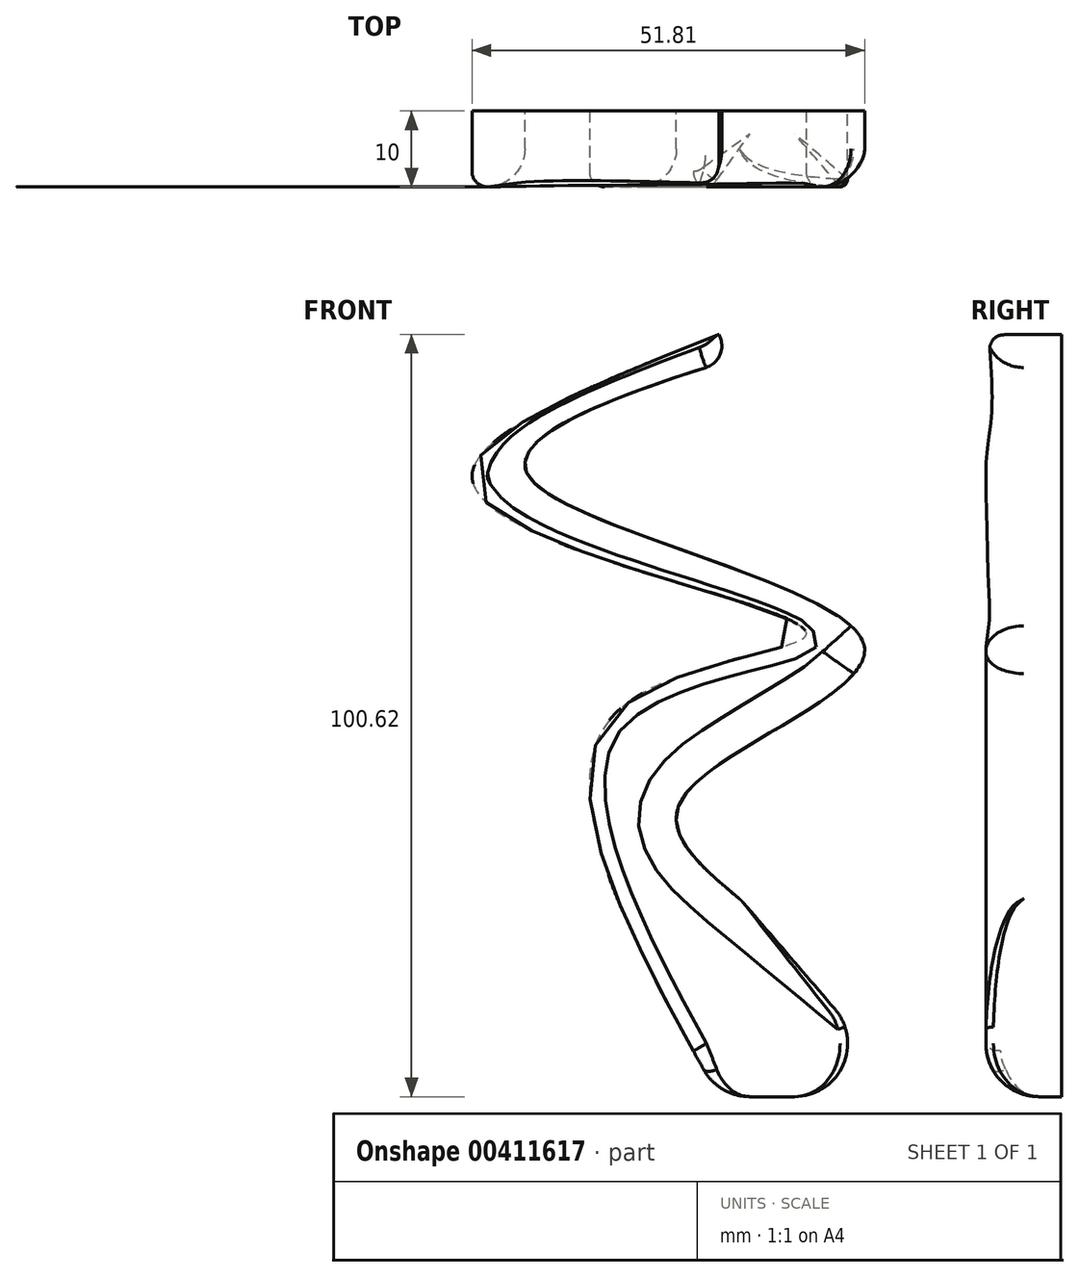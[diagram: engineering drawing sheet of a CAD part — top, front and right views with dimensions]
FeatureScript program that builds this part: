
annotation { "Feature Type Name" : "Feature", "Feature Type Description" : "" }
export const myFeature = defineFeature(function(context is Context, id is Id, definition is map)
    precondition{}
    {
        {
            var Q0;
            Q0=qCreatedBy(makeId("Front.planeOp"),FACE);
            var sketch = newSketch(context, id + "F0", { "sketchPlane" : qUnion([Q0])});
            skFitSpline(sketch, "E0", {"points": [v(0, 0) * mm, v(-32.55, -18.47) * mm, v(-11.86, -30.76) * mm, v(11.43, -39.81) * mm, v(-13.8, -50.16) * mm, v(0, -100.62) * mm], "startDerivative": vector(-224.38, -89.25) * mm, "endDerivative": vector(135.1, -241.68) * mm});
            skLineSegment(sketch, "E1", {"start": v(0, -100.62) * mm, "end": v(25.25, -100.62) * mm});
            skLineSegment(sketch, "E2", {"start": v(25.25, -100.62) * mm, "end": v(3.02, -74.74) * mm});
            skPoint(sketch, "E3.4.internal.snap0", {"position": v(12.63, -64.84) * mm});
            skFitSpline(sketch, "E3", {"points": [v(3.02, -74.74) * mm, v(-4.74, -61.16) * mm, v(19.2, -41.1) * mm, v(-24.8, -19.12) * mm, v(12.63, 0) * mm], "startDerivative": vector(-94.06, 77.83) * mm, "endDerivative": vector(227.32, 67.7) * mm});
            skLineSegment(sketch, "E4", {"start": v(0, 0) * mm, "end": v(12.63, 0) * mm});
            skSolve(sketch);
        }
        {
            var Q0;
            Q0=makeQuery(id+"F0.imprint","IMPRINT",FACE,{"disambiguationData":[TD([[makeQuery(id+"F0.imprint","IMPRINT",EDGE,{"derivedFrom":sQuery(id+"F0.wireOp",EDGE,"E0")}),1.0]])]});
            extrude(context, id + "F1", {"entities" : qUnion([Q0]), "depth" : 10 * mm});
        }
        {
            var Q0;
            Q0=makeQuery(id+"F1.opExtrude","CAP_EDGE",EDGE,{"disambiguationData":[OSD([sQuery(id+"F0.wireOp",EDGE,"E2")])],"isStart":false});
            fillet(context, id + "F2", {"entities" : qUnion([Q0]), "radius" : 1 * mm, "tangentPropagation" : true, "allowEdgeOverflow" : false});
        }
        {
            var Q0;
            Q0=makeQuery(id+"F1.opExtrude","CAP_EDGE",EDGE,{"disambiguationData":[OSD([sQuery(id+"F0.wireOp",EDGE,"E0")])],"isStart":false});
            fillet(context, id + "F3", {"entities" : qUnion([Q0]), "radius" : 2 * mm, "tangentPropagation" : true, "allowEdgeOverflow" : false});
        }
        {
            var Q0;
            Q0=makeQuery(id+"F1.opExtrude","CAP_EDGE",EDGE,{"disambiguationData":[OSD([sQuery(id+"F0.wireOp",EDGE,"E3")])],"isStart":false});
            fillet(context, id + "F4", {"entities" : qUnion([Q0]), "radius" : 5 * mm, "tangentPropagation" : true, "allowEdgeOverflow" : false});
        }
        {
            var Q0;
            Q0=makeQuery(id+"F1.opExtrude","CAP_EDGE",EDGE,{"disambiguationData":[OSD([sQuery(id+"F0.wireOp",EDGE,"E1")])],"isStart":false});
            fillet(context, id + "F5", {"entities" : qUnion([Q0]), "radius" : 7 * mm, "tangentPropagation" : true, "allowEdgeOverflow" : false});
        }
        {
            var Q0;
            Q0=makeQuery(id+"F4.opFillet","BLEND_EDGE",EDGE,{"blendedFrom":[makeQuery(id+"F1.opExtrude","CAP_EDGE",EDGE,{"disambiguationData":[OSD([sQuery(id+"F0.wireOp",EDGE,"E3")])],"isStart":false}),makeQuery(id+"F1.opExtrude","SWEPT_FACE",FACE,{"disambiguationData":[OSD([sQuery(id+"F0.wireOp",EDGE,"E4")])]})],"blendedInto":[makeQuery(id+"F1.opExtrude","SWEPT_FACE",FACE,{"disambiguationData":[OSD([sQuery(id+"F0.wireOp",EDGE,"E4")])]})]});
            fillet(context, id + "F6", {"entities" : qUnion([Q0]), "radius" : 3 * mm, "tangentPropagation" : true, "allowEdgeOverflow" : false});
        }
    });
